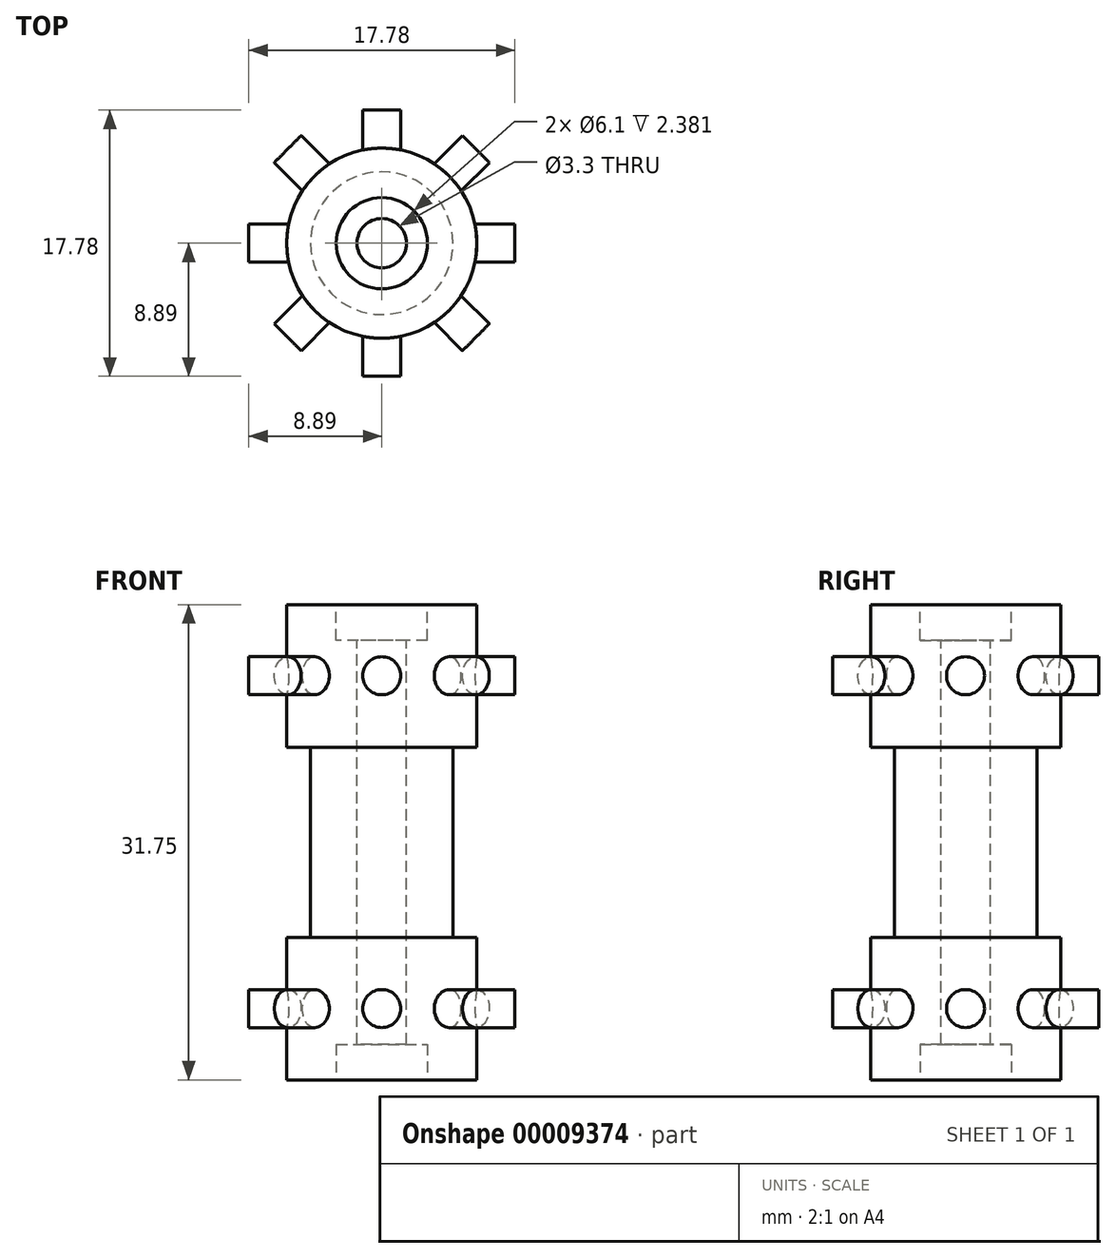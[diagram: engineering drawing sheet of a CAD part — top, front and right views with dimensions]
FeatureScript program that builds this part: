
annotation { "Feature Type Name" : "Feature", "Feature Type Description" : "" }
export const myFeature = defineFeature(function(context is Context, id is Id, definition is map)
    precondition{}
    {
        {
            var Q0;
            Q0=qCreatedBy(makeId("Top.planeOp"),FACE);
            var sketch = newSketch(context, id + "F0", { "sketchPlane" : qUnion([Q0])});
            skCircle(sketch, "E0", {"center": v(0, 0) * mm, "radius": 6.35 * mm});
            skCircle(sketch, "E1", {"center": v(0, 0) * mm, "radius": 4.76 * mm});
            skSolve(sketch);
        }
        {
            var Q0;
            Q0=makeQuery(id+"F0.imprint","IMPRINT",FACE,{"disambiguationData":[TD([[makeQuery(id+"F0.imprint","IMPRINT",EDGE,{"derivedFrom":sQuery(id+"F0.wireOp",EDGE,"E1")}),1.0]])]});
            extrude(context, id + "F1", {"entities" : qUnion([Q0]), "depth" : 31.75 * mm});
        }
        {
            var Q0;
            Q0=makeQuery(id+"F0.imprint","IMPRINT",FACE,{"disambiguationData":[TD([[makeQuery(id+"F0.imprint","IMPRINT",EDGE,{"derivedFrom":sQuery(id+"F0.wireOp",EDGE,"E0")}),1.0]])]});
            extrude(context, id + "F2", {"entities" : qUnion([Q0]), "operationType" : NewBodyOperationType.ADD, "depth" : 9.52 * mm});
        }
        {
            var Q0;
            Q0=makeQuery(id+"F1.opExtrude","CAP_FACE",FACE,{"disambiguationData":[OSD([sQuery(id+"F0.wireOp",EDGE,"E1")])],"isStart":false});
            var sketch = newSketch(context, id + "F3", { "sketchPlane" : qUnion([Q0])});
            skCircle(sketch, "E2", {"center": v(0, 0) * mm, "radius": 6.35 * mm});
            skSolve(sketch);
        }
        {
            var Q0;
            Q0=makeQuery(id+"F3.imprint","IMPRINT",FACE,{"disambiguationData":[TD([[makeQuery(id+"F3.imprint","IMPRINT",EDGE,{"derivedFrom":sQuery(id+"F3.wireOp",EDGE,"E2")}),1.0]])]});
            extrude(context, id + "F4", {"entities" : qUnion([Q0]), "operationType" : NewBodyOperationType.ADD, "oppositeDirection" : true, "depth" : 9.52 * mm});
        }
        {
            var Q0;
            {var subQ0=sQuery(id+"F0.wireOp",EDGE,"E1");Q0=makeQuery(id+"F4.boolean.opBoolean","MERGE",FACE,{"derivedFrom":[makeQuery(id+"F1.opExtrude","CAP_FACE",FACE,{"disambiguationData":[OSD([subQ0])],"isStart":false}),makeQuery(id+"F4.opExtrude","CAP_FACE",FACE,{"disambiguationData":[OSD([subQ0,sQuery(id+"F3.wireOp",EDGE,"E2")])],"isStart":true})]});}
            var sketch = newSketch(context, id + "F5", { "sketchPlane" : qUnion([Q0])});
            skCircle(sketch, "E3", {"center": v(0, 0) * mm, "radius": 1.65 * mm});
            skSolve(sketch);
        }
        {
            var Q0;
            Q0=makeQuery(id+"F5.imprint","IMPRINT",FACE,{"disambiguationData":[TD([[makeQuery(id+"F5.imprint","IMPRINT",EDGE,{"derivedFrom":sQuery(id+"F5.wireOp",EDGE,"E3")}),1.0]])]});
            extrude(context, id + "F6", {"entities" : qUnion([Q0]), "operationType" : NewBodyOperationType.REMOVE, "oppositeDirection" : true, "depth" : 34.2 * mm});
        }
        {
            var Q0;
            Q0=qCreatedBy(makeId("Front.planeOp"),FACE);
            cPlane(context, id + "F7", {"entities" : qUnion([Q0]), "cplaneType" : CPlaneType.OFFSET, "offset" : 6.35 * mm, "width" : 152.4 * mm, "height" : 152.4 * mm});
        }
        {
            var Q0;
            Q0=qCreatedBy(id+"F7.planeOp",FACE);
            var sketch = newSketch(context, id + "F8", { "sketchPlane" : qUnion([Q0])});
            skLineSegment(sketch, "E4", {"start": v(0, 0) * mm, "end": v(0, 31.76) * mm});
            skLineSegment(sketch, "E5", {"start": v(0, 31.76) * mm, "end": v(0, 27) * mm});
            skCircle(sketch, "E6", {"center": v(0, 27) * mm, "radius": 1.27 * mm});
            skSolve(sketch);
        }
        {
            var Q0;
            {var subQ1=sQuery(id+"F8.wireOp",EDGE,"E5");var subQ3=sQuery(id+"F8.wireOp",EDGE,"E4");var subQ5=makeQuery(id+"F8.imprint","INTERSECT",VERTEX,{"derivedFrom":[subQ3,subQ1]});Q0=makeQuery(id+"F8.imprint","IMPRINT",FACE,{"disambiguationData":[TD([[makeQuery(id+"F8.imprint","IMPRINT",EDGE,{"disambiguationData":[TD([[subQ5,1.0]])],"derivedFrom":subQ3}),-1.0]])]});}
            var Q1;
            {var subQ1=sQuery(id+"F8.wireOp",EDGE,"E5");var subQ3=sQuery(id+"F8.wireOp",EDGE,"E4");var subQ5=makeQuery(id+"F8.imprint","INTERSECT",VERTEX,{"derivedFrom":[subQ3,subQ1]});Q1=makeQuery(id+"F8.imprint","IMPRINT",FACE,{"disambiguationData":[TD([[makeQuery(id+"F8.imprint","IMPRINT",EDGE,{"disambiguationData":[TD([[subQ5,1.0]])],"derivedFrom":subQ3}),1.0]])]});}
            extrude(context, id + "F9", {"entities" : qUnion([Q0, Q1]), "operationType" : NewBodyOperationType.ADD, "depth" : 2.54 * mm, "hasSecondDirection" : true, "secondDirectionOppositeDirection" : true, "secondDirectionDepth" : 0.25 * mm});
        }
        {
            var Q0;
            Q0=makeQuery(id+"F9.opExtrude","SWEPT_FACE",FACE,{"disambiguationData":[OSD([sQuery(id+"F8.wireOp",EDGE,"E6")])]});
            var Q1;
            Q1=makeQuery(id+"F9.opExtrude","CAP_FACE",FACE,{"disambiguationData":[OSD([sQuery(id+"F8.wireOp",EDGE,"E6")])],"isStart":false});
            var Q2;
            Q2=makeQuery(id+"F4.opExtrude","SWEPT_FACE",FACE,{"disambiguationData":[OSD([sQuery(id+"F3.wireOp",EDGE,"E2")])]});
            circularPattern(context, id + "F10", {"faces" : qUnion([Q0, Q1]), "axis" : qUnion([Q2]), "angle" : 45 * degree, "instanceCount" : 8, "patternType" : PatternType.FACE});
        }
        {
            var Q0;
            Q0=qCreatedBy(id+"F7.planeOp",FACE);
            var sketch = newSketch(context, id + "F11", { "sketchPlane" : qUnion([Q0])});
            skCircle(sketch, "E7", {"center": v(0, 4.76) * mm, "radius": 1.27 * mm});
            skSolve(sketch);
        }
        {
            var Q0;
            Q0=makeQuery(id+"F11.imprint","IMPRINT",FACE,{"disambiguationData":[TD([[makeQuery(id+"F11.imprint","IMPRINT",EDGE,{"derivedFrom":sQuery(id+"F11.wireOp",EDGE,"E7")}),1.0]])]});
            extrude(context, id + "F12", {"entities" : qUnion([Q0]), "operationType" : NewBodyOperationType.ADD, "depth" : 2.54 * mm, "hasSecondDirection" : true, "secondDirectionOppositeDirection" : true, "secondDirectionDepth" : 0.25 * mm});
        }
        {
            var Q0;
            Q0=makeQuery(id+"F12.opExtrude","CAP_FACE",FACE,{"disambiguationData":[OSD([sQuery(id+"F11.wireOp",EDGE,"E7")])],"isStart":false});
            var Q1;
            Q1=makeQuery(id+"F12.opExtrude","SWEPT_FACE",FACE,{"disambiguationData":[OSD([sQuery(id+"F11.wireOp",EDGE,"E7")])]});
            var Q2;
            Q2=makeQuery(id+"F2.opExtrude","SWEPT_FACE",FACE,{"disambiguationData":[OSD([sQuery(id+"F0.wireOp",EDGE,"E0")])]});
            circularPattern(context, id + "F13", {"faces" : qUnion([Q0, Q1]), "axis" : qUnion([Q2]), "angle" : 45 * degree, "instanceCount" : 8, "patternType" : PatternType.FACE});
        }
        {
            var Q0;
            {var subQ0=sQuery(id+"F0.wireOp",EDGE,"E1");Q0=makeQuery(id+"F4.boolean.opBoolean","MERGE",FACE,{"derivedFrom":[makeQuery(id+"F1.opExtrude","CAP_FACE",FACE,{"disambiguationData":[OSD([subQ0])],"isStart":false}),makeQuery(id+"F4.opExtrude","CAP_FACE",FACE,{"disambiguationData":[OSD([subQ0,sQuery(id+"F3.wireOp",EDGE,"E2")])],"isStart":true})]});}
            var sketch = newSketch(context, id + "F14", { "sketchPlane" : qUnion([Q0])});
            skCircle(sketch, "E8", {"center": v(0, 0) * mm, "radius": 3.05 * mm});
            skSolve(sketch);
        }
        {
            var Q0;
            Q0=makeQuery(id+"F14.imprint","IMPRINT",FACE,{"disambiguationData":[TD([[makeQuery(id+"F14.imprint","IMPRINT",EDGE,{"derivedFrom":sQuery(id+"F14.wireOp",EDGE,"E8")}),1.0]])]});
            extrude(context, id + "F15", {"entities" : qUnion([Q0]), "operationType" : NewBodyOperationType.REMOVE, "oppositeDirection" : true, "depth" : 2.38 * mm});
        }
        {
            var Q0;
            {var subQ0=sQuery(id+"F0.wireOp",EDGE,"E1");Q0=makeQuery(id+"F2.boolean.opBoolean","MERGE",FACE,{"derivedFrom":[makeQuery(id+"F1.opExtrude","CAP_FACE",FACE,{"disambiguationData":[OSD([subQ0])],"isStart":true}),makeQuery(id+"F2.opExtrude","CAP_FACE",FACE,{"disambiguationData":[OSD([sQuery(id+"F0.wireOp",EDGE,"E0"),subQ0])],"isStart":true})]});}
            var sketch = newSketch(context, id + "F16", { "sketchPlane" : qUnion([Q0])});
            skCircle(sketch, "E9", {"center": v(0, 0) * mm, "radius": 3.05 * mm});
            skSolve(sketch);
        }
        {
            var Q0;
            Q0=makeQuery(id+"F16.imprint","IMPRINT",FACE,{"disambiguationData":[TD([[makeQuery(id+"F16.imprint","IMPRINT",EDGE,{"derivedFrom":sQuery(id+"F16.wireOp",EDGE,"E9")}),1.0]])]});
            extrude(context, id + "F17", {"entities" : qUnion([Q0]), "operationType" : NewBodyOperationType.REMOVE, "oppositeDirection" : true, "depth" : 2.38 * mm});
        }
    });
